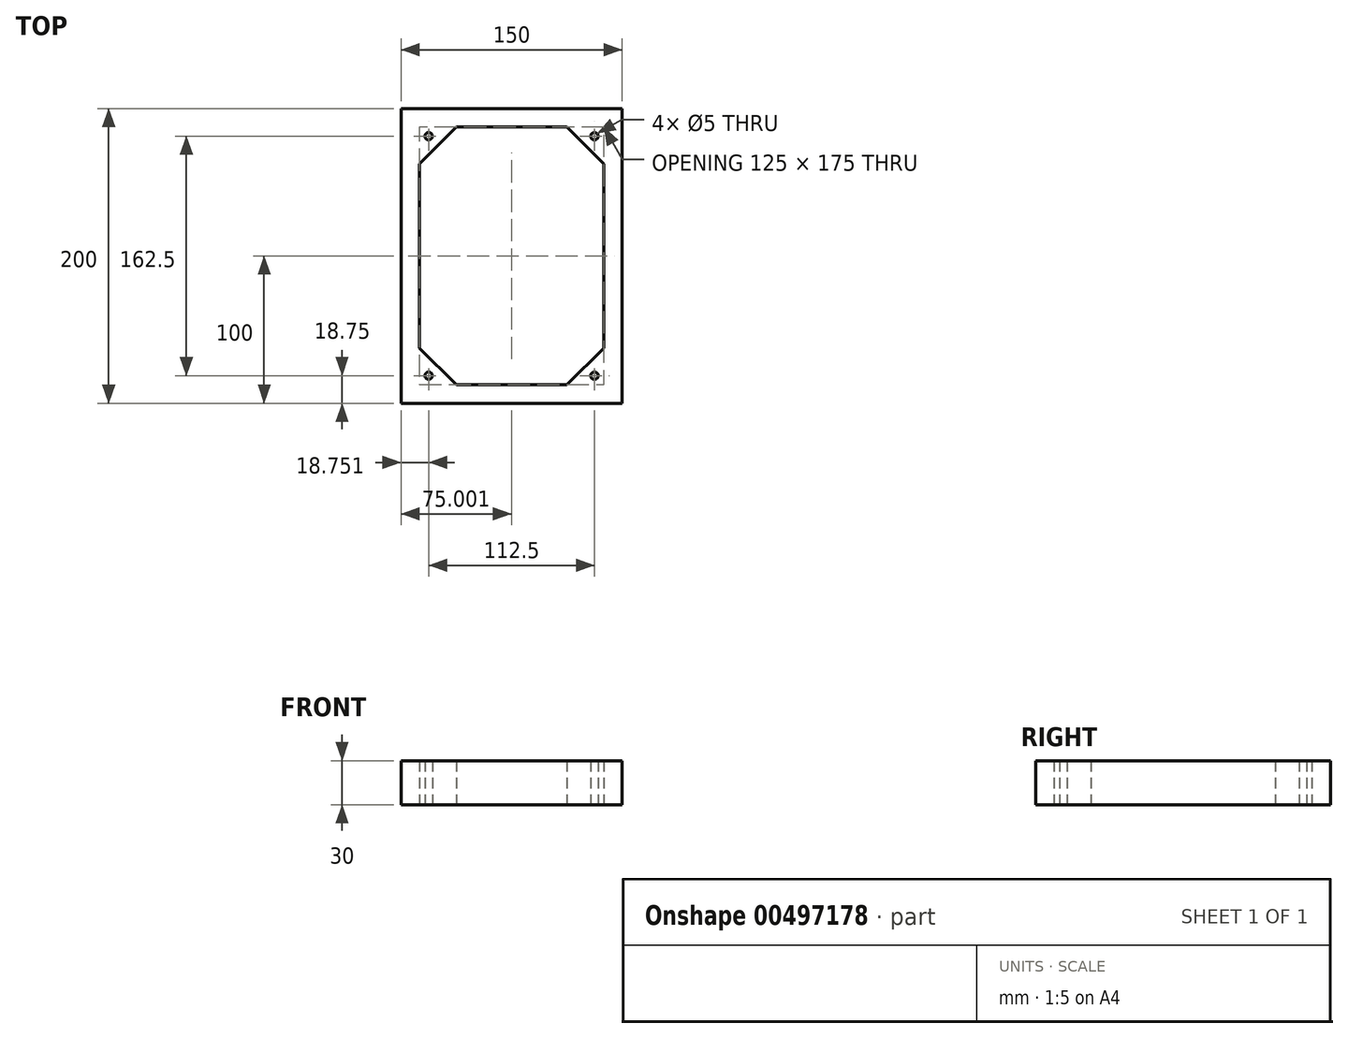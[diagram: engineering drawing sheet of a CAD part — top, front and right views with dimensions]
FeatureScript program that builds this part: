
annotation { "Feature Type Name" : "Feature", "Feature Type Description" : "" }
export const myFeature = defineFeature(function(context is Context, id is Id, definition is map)
    precondition{}
    {
        {
            var Q0;
            Q0=qCreatedBy(makeId("Top.planeOp"),FACE);
            var sketch = newSketch(context, id + "F0", { "sketchPlane" : qUnion([Q0])});
            skLineSegment(sketch, "E0.bottom", {"start": v(-75.07, 100) * mm, "end": v(74.93, 100) * mm});
            skLineSegment(sketch, "E0.top", {"start": v(-75.07, -100) * mm, "end": v(74.93, -100) * mm});
            skLineSegment(sketch, "E0.left", {"start": v(-75.07, 100) * mm, "end": v(-75.07, -100) * mm});
            skLineSegment(sketch, "E0.right", {"start": v(74.93, 100) * mm, "end": v(74.93, -100) * mm});
            skLineSegment(sketch, "E1.bottom", {"start": v(-68.82, 93.75) * mm, "end": v(68.68, 93.75) * mm});
            skLineSegment(sketch, "E1.top", {"start": v(-68.82, -93.75) * mm, "end": v(68.68, -93.75) * mm});
            skLineSegment(sketch, "E1.left", {"start": v(-68.82, 93.75) * mm, "end": v(-68.82, -93.75) * mm});
            skLineSegment(sketch, "E1.right", {"start": v(68.68, 93.75) * mm, "end": v(68.68, -93.75) * mm});
            skLineSegment(sketch, "E2.bottom", {"start": v(-62.57, 87.5) * mm, "end": v(62.43, 87.5) * mm});
            skLineSegment(sketch, "E2.top", {"start": v(-62.57, -87.5) * mm, "end": v(62.43, -87.5) * mm});
            skLineSegment(sketch, "E2.left", {"start": v(-62.57, 87.5) * mm, "end": v(-62.57, -87.5) * mm});
            skLineSegment(sketch, "E2.right", {"start": v(62.43, 87.5) * mm, "end": v(62.43, -87.5) * mm});
            skPoint(sketch, "E3", {"position": v(37.43, 87.5) * mm});
            skPoint(sketch, "E4", {"position": v(37.43, -87.5) * mm});
            skPoint(sketch, "E5", {"position": v(-37.57, 87.5) * mm});
            skPoint(sketch, "E6", {"position": v(-37.57, -87.5) * mm});
            skPoint(sketch, "E7", {"position": v(-62.57, 62.5) * mm});
            skPoint(sketch, "E8", {"position": v(62.43, 62.5) * mm});
            skPoint(sketch, "E9", {"position": v(62.43, -62.5) * mm});
            skPoint(sketch, "E10", {"position": v(-62.57, -62.5) * mm});
            skPoint(sketch, "E11", {"position": v(-62.57, 87.5) * mm});
            skPoint(sketch, "E12", {"position": v(62.43, 87.5) * mm});
            skPoint(sketch, "E13", {"position": v(62.43, -87.5) * mm});
            skPoint(sketch, "E14", {"position": v(-62.57, -87.5) * mm});
            skLineSegment(sketch, "E15", {"start": v(-62.57, -62.5) * mm, "end": v(-37.57, -87.5) * mm});
            skLineSegment(sketch, "E16", {"start": v(37.43, -87.5) * mm, "end": v(62.43, -62.5) * mm});
            skLineSegment(sketch, "E17", {"start": v(62.43, 62.5) * mm, "end": v(37.43, 87.5) * mm});
            skLineSegment(sketch, "E18", {"start": v(-37.57, 87.5) * mm, "end": v(-62.57, 62.5) * mm});
            skPoint(sketch, "E19", {"position": v(-50.07, 75) * mm});
            skPoint(sketch, "E20", {"position": v(49.93, 75) * mm});
            skPoint(sketch, "E21", {"position": v(49.93, -75) * mm});
            skPoint(sketch, "E22", {"position": v(-50.07, -75) * mm});
            skLineSegment(sketch, "E23", {"start": v(-62.57, 87.5) * mm, "end": v(-50.07, 75) * mm, "construction": true});
            skLineSegment(sketch, "E24", {"start": v(62.43, 87.5) * mm, "end": v(49.93, 75) * mm, "construction": true});
            skLineSegment(sketch, "E25", {"start": v(62.43, -87.5) * mm, "end": v(49.93, -75) * mm, "construction": true});
            skLineSegment(sketch, "E26", {"start": v(-62.57, -87.5) * mm, "end": v(-50.07, -75) * mm, "construction": true});
            skPoint(sketch, "E27", {"position": v(-56.32, 81.25) * mm});
            skPoint(sketch, "E28", {"position": v(56.18, 81.25) * mm});
            skPoint(sketch, "E29", {"position": v(56.18, -81.25) * mm});
            skPoint(sketch, "E30", {"position": v(-56.32, -81.25) * mm});
            skCircle(sketch, "E31", {"center": v(-56.32, -81.25) * mm, "radius": 2.5 * mm});
            skCircle(sketch, "E32", {"center": v(56.18, -81.25) * mm, "radius": 2.5 * mm});
            skCircle(sketch, "E33", {"center": v(56.18, 81.25) * mm, "radius": 2.5 * mm});
            skCircle(sketch, "E34", {"center": v(-56.32, 81.25) * mm, "radius": 2.5 * mm});
            skCircle(sketch, "E35", {"center": v(-56.32, 81.25) * mm, "radius": 5 * mm});
            skCircle(sketch, "E36", {"center": v(56.18, 81.25) * mm, "radius": 5 * mm});
            skCircle(sketch, "E37", {"center": v(-56.32, -81.25) * mm, "radius": 5 * mm});
            skCircle(sketch, "E38", {"center": v(56.18, -81.25) * mm, "radius": 5 * mm});
            skSolve(sketch);
        }
        {
            var Q0;
            Q0=makeQuery(id+"F0.imprint","IMPRINT",FACE,{"disambiguationData":[TD([[makeQuery(id+"F0.imprint","IMPRINT",EDGE,{"derivedFrom":sQuery(id+"F0.wireOp",EDGE,"E0.bottom")}),-1.0]])]});
            var Q1;
            Q1=makeQuery(id+"F0.imprint","IMPRINT",FACE,{"disambiguationData":[TD([[makeQuery(id+"F0.imprint","IMPRINT",EDGE,{"derivedFrom":sQuery(id+"F0.wireOp",EDGE,"E1.bottom")}),-1.0]])]});
            var Q2;
            {var subQ3=sQuery(id+"F0.wireOp",EDGE,"E18");Q2=makeQuery(id+"F0.imprint","IMPRINT",FACE,{"disambiguationData":[TD([[makeQuery(id+"F0.imprint","IMPRINT",EDGE,{"derivedFrom":subQ3}),-1.0]])]});}
            var Q3;
            {var subQ3=sQuery(id+"F0.wireOp",EDGE,"E17");Q3=makeQuery(id+"F0.imprint","IMPRINT",FACE,{"disambiguationData":[TD([[makeQuery(id+"F0.imprint","IMPRINT",EDGE,{"derivedFrom":subQ3}),-1.0]])]});}
            var Q4;
            Q4=makeQuery(id+"F0.imprint","IMPRINT",FACE,{"disambiguationData":[TD([[makeQuery(id+"F0.imprint","IMPRINT",EDGE,{"derivedFrom":sQuery(id+"F0.wireOp",EDGE,"E34")}),-1.0]])]});
            var Q5;
            Q5=makeQuery(id+"F0.imprint","IMPRINT",FACE,{"disambiguationData":[TD([[makeQuery(id+"F0.imprint","IMPRINT",EDGE,{"derivedFrom":sQuery(id+"F0.wireOp",EDGE,"E33")}),-1.0]])]});
            var Q6;
            {var subQ3=sQuery(id+"F0.wireOp",EDGE,"E16");Q6=makeQuery(id+"F0.imprint","IMPRINT",FACE,{"disambiguationData":[TD([[makeQuery(id+"F0.imprint","IMPRINT",EDGE,{"derivedFrom":subQ3}),-1.0]])]});}
            var Q7;
            Q7=makeQuery(id+"F0.imprint","IMPRINT",FACE,{"disambiguationData":[TD([[makeQuery(id+"F0.imprint","IMPRINT",EDGE,{"derivedFrom":sQuery(id+"F0.wireOp",EDGE,"E32")}),-1.0]])]});
            var Q8;
            Q8=makeQuery(id+"F0.imprint","IMPRINT",FACE,{"disambiguationData":[TD([[makeQuery(id+"F0.imprint","IMPRINT",EDGE,{"derivedFrom":sQuery(id+"F0.wireOp",EDGE,"E31")}),-1.0]])]});
            var Q9;
            {var subQ3=sQuery(id+"F0.wireOp",EDGE,"E15");Q9=makeQuery(id+"F0.imprint","IMPRINT",FACE,{"disambiguationData":[TD([[makeQuery(id+"F0.imprint","IMPRINT",EDGE,{"derivedFrom":subQ3}),-1.0]])]});}
            extrude(context, id + "F1", {"entities" : qUnion([Q0, Q1, Q2, Q3, Q4, Q5, Q6, Q7, Q8, Q9]), "depth" : 30 * mm, "offsetDistance" : 25 * mm});
        }
    });
